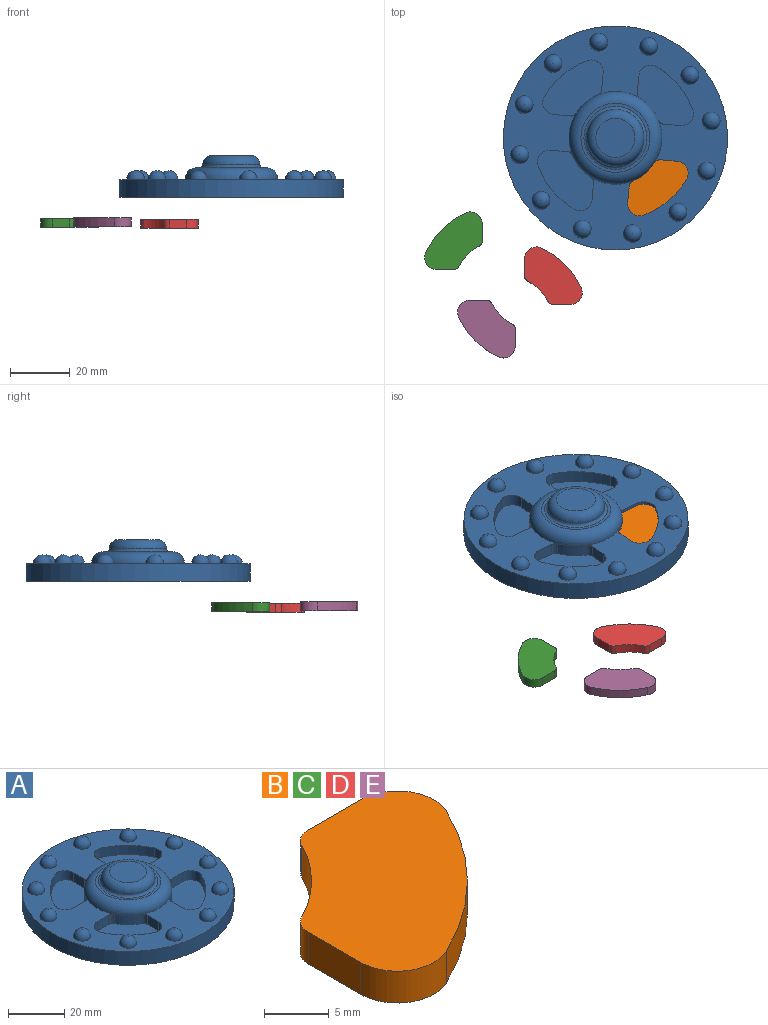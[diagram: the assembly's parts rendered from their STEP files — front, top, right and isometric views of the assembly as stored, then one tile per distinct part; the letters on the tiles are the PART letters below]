
ASSEMBLY  parts=5 mates=1
PART A: 56 faces, bbox 75.1x75.1x14 mm
  f0: cylinder r=15.56mm len=6.77mm, axis (0,0,-1), area 38.9mm2, adj f19,f27,f52,f55
  f1: cylinder r=15.56mm len=6.77mm, axis (0,0,-1), area 38.9mm2, adj f20,f27,f51,f54
  f2: cylinder r=15.56mm len=6.77mm, axis (0,0,-1), area 38.9mm2, adj f21,f27,f49,f50
  f3: cylinder r=37.56mm len=75.13mm, axis (0,0,-1), area 1416.2mm2, adj f4,f18
  f4: plane 75.13x75.13mm, normal (0,0,-1), area 4433.2mm2, adj f3
  f5: plane 5.7x4mm, normal (1,0,0), area 22.8mm2, adj f18,f22,f46,f48
  f6: cylinder r=27.56mm len=13.26mm, axis (0,0,-1), area 76.6mm2, adj f18,f22,f46,f47
  f7: plane 5.7x4mm, normal (0,1,0), area 22.8mm2, adj f18,f22,f47,f53
  f8: cylinder r=27.56mm len=13.26mm, axis (0,0,-1), area 76.6mm2, adj f18,f21,f44,f45
  f9: plane 5.7x4mm, normal (-1,0,0), area 22.8mm2, adj f18,f21,f45,f49
  f10: cylinder r=15.56mm len=6.77mm, axis (0,0,-1), area 38.9mm2, adj f22,f27,f48,f53
  f11: cylinder r=27.56mm len=13.26mm, axis (0,0,-1), area 76.6mm2, adj f18,f20,f42,f43
  f12: plane 5.7x4mm, normal (0,-1,0), area 22.8mm2, adj f18,f20,f43,f51
  f13: cylinder r=27.56mm len=13.26mm, axis (0,0,-1), area 76.6mm2, adj f18,f19,f40,f41
  f14: plane 5.7x4mm, normal (1,0,0), area 22.8mm2, adj f18,f19,f41,f55
  f15: plane 5.7x4mm, normal (0,1,0), area 22.8mm2, adj f18,f21,f44,f50
  f16: plane 5.7x4mm, normal (-1,0,0), area 22.8mm2, adj f18,f20,f42,f54
  f17: plane 5.7x4mm, normal (0,-1,0), area 22.8mm2, adj f18,f19,f40,f52
  f18: plane 75.13x75.13mm, normal (0,0,1), area 2354.9mm2, adj f3,f5,f6,f7,f8,f9,f11,f12
  f19: plane 19.34x19.34mm, normal (0,0,1), area 244.5mm2, adj f0,f13,f14,f17,f40,f41,f52,f55
  f20: plane 19.34x19.34mm, normal (0,0,1), area 244.5mm2, adj f1,f11,f12,f16,f42,f43,f51,f54
  f21: plane 19.34x19.34mm, normal (0,0,1), area 244.5mm2, adj f2,f8,f9,f15,f44,f45,f49,f50
  f22: plane 19.34x19.34mm, normal (0,0,1), area 244.5mm2, adj f5,f6,f7,f10,f46,f47,f48,f53
  f23: plane 23.13x23.13mm, normal (0,0,1), area 69.5mm2, adj f26,f27
  f24: plane 13.13x13.13mm, normal (0,0,1), area 135.4mm2, adj f25
  f25: torus R=6.56mm, axis (0,0,1), area 250.9mm2, adj f24,f26
  f26: torus R=10.56mm, axis (0,0,1), area 98mm2, adj f23,f25
  f27: torus R=11.56mm, axis (0,0,1), area 557.1mm2, adj f0,f1,f2,f10,f18,f23
  f28: sphere r=3mm, area 56.5mm2, adj f18
  f29: sphere r=3mm, area 56.5mm2, adj f18
  f30: sphere r=3mm, area 56.5mm2, adj f18
  f31: sphere r=3mm, area 56.5mm2, adj f18
  f32: sphere r=3mm, area 56.5mm2, adj f18
  f33: sphere r=3mm, area 56.5mm2, adj f18
  f34: sphere r=3mm, area 56.5mm2, adj f18
  f35: sphere r=3mm, area 56.5mm2, adj f18
  f36: sphere r=3mm, area 56.5mm2, adj f18
  f37: sphere r=3mm, area 56.5mm2, adj f18
  f38: sphere r=3mm, area 56.5mm2, adj f18
  f39: sphere r=3mm, area 56.5mm2, adj f18
  f40: cylinder r=4mm len=5.7mm, axis (0,0,-1), area 32.1mm2, adj f13,f17,f18,f19
  f41: cylinder r=4mm len=5.7mm, axis (0,0,-1), area 32.1mm2, adj f13,f14,f18,f19
  f42: cylinder r=4mm len=5.7mm, axis (0,0,-1), area 32.1mm2, adj f11,f16,f18,f20
  f43: cylinder r=4mm len=5.7mm, axis (0,0,-1), area 32.1mm2, adj f11,f12,f18,f20
  f44: cylinder r=4mm len=5.7mm, axis (0,0,-1), area 32.1mm2, adj f8,f15,f18,f21
  f45: cylinder r=4mm len=5.7mm, axis (0,0,-1), area 32.1mm2, adj f8,f9,f18,f21
  f46: cylinder r=4mm len=5.7mm, axis (0,0,-1), area 32.1mm2, adj f5,f6,f18,f22
  f47: cylinder r=4mm len=5.7mm, axis (0,0,-1), area 32.1mm2, adj f6,f7,f18,f22
  f48: cylinder r=2mm len=4mm, axis (0,0,-1), area 8.8mm2, adj f5,f10,f18,f22
  f49: cylinder r=2mm len=4mm, axis (0,0,-1), area 8.8mm2, adj f2,f9,f18,f21
  f50: cylinder r=2mm len=4mm, axis (0,0,-1), area 8.8mm2, adj f2,f15,f18,f21
  f51: cylinder r=2mm len=4mm, axis (0,0,-1), area 8.8mm2, adj f1,f12,f18,f20
  f52: cylinder r=2mm len=4mm, axis (0,0,-1), area 8.8mm2, adj f0,f17,f18,f19
  f53: cylinder r=2mm len=4mm, axis (0,0,-1), area 8.8mm2, adj f7,f10,f18,f22
  f54: cylinder r=2mm len=4mm, axis (0,0,-1), area 8.8mm2, adj f1,f16,f18,f20
  f55: cylinder r=2mm len=4mm, axis (0,0,-1), area 8.8mm2, adj f0,f14,f18,f19
PART B: 10 faces, bbox 19.3x19.3x3 mm
  f0: cylinder r=27.56mm len=13.26mm, axis (0,0,-1), area 57.4mm2, adj f4,f5,f6,f7
  f1: plane 5.7x3mm, normal (0,1,0), area 17.1mm2, adj f4,f5,f6,f8
  f2: cylinder r=15.56mm len=6.77mm, axis (0,0,-1), area 29.2mm2, adj f4,f5,f8,f9
  f3: plane 5.7x3mm, normal (-1,0,0), area 17.1mm2, adj f4,f5,f7,f9
  f4: plane 19.34x19.34mm, normal (0,0,1), area 244.5mm2, adj f0,f1,f2,f3,f6,f7,f8,f9
  f5: plane 19.34x19.34mm, normal (0,0,-1), area 244.5mm2, adj f0,f1,f2,f3,f6,f7,f8,f9
  f6: cylinder r=4mm len=5.7mm, axis (0,0,-1), area 24.1mm2, adj f0,f1,f4,f5
  f7: cylinder r=4mm len=5.7mm, axis (0,0,-1), area 24.1mm2, adj f0,f3,f4,f5
  f8: cylinder r=2mm len=3mm, axis (0,0,-1), area 6.6mm2, adj f1,f2,f4,f5
  f9: cylinder r=2mm len=3mm, axis (0,0,-1), area 6.6mm2, adj f2,f3,f4,f5
PART C: same geometry as B
PART D: same geometry as B
PART E: same geometry as B
PLACE A rot(axis=(0,0,-1),5deg) t=(9.93,4.31,8.21)mm
PLACE B rot(axis=(0,0,-1),5deg) t=(-37.29,8.44,10.21)mm
PLACE C rot(axis=(0,0,1),180deg) t=(18.7,-45.83,-1.86)mm
PLACE D rot(axis=(0,0,1),90deg) t=(-26.53,-104.95,-2.15)mm
PLACE E rot(axis=(0,0,-1),90deg) t=(-17.66,3.3,-1.59)mm
MATE fastened B.f5 <-> A.f19  axis (0,0,-1) through (23.67,-12.06,10.21)mm
